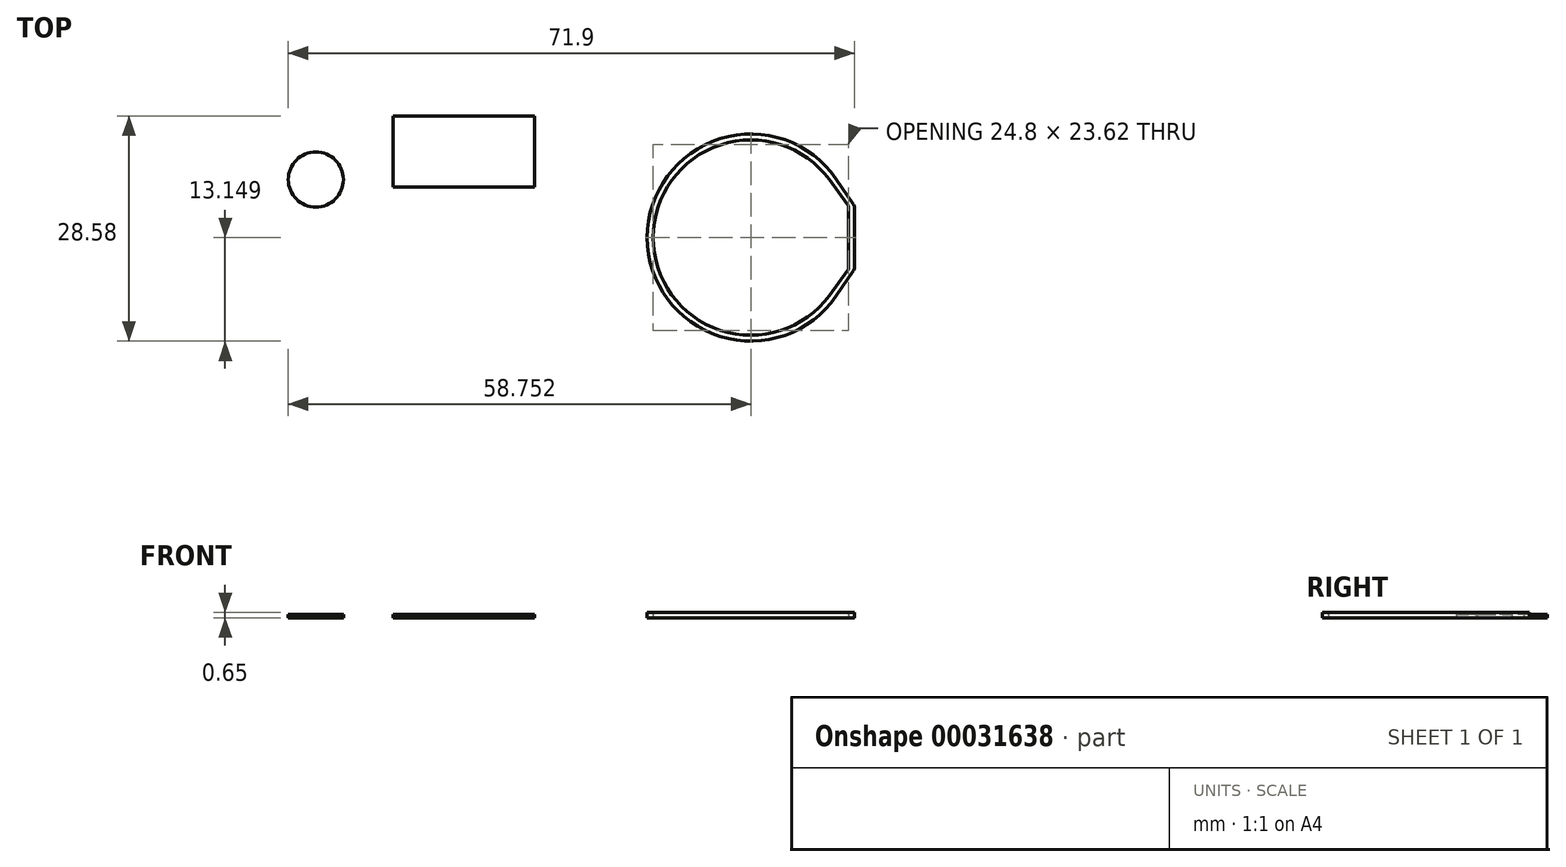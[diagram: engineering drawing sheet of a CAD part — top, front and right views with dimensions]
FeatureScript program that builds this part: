
annotation { "Feature Type Name" : "Feature", "Feature Type Description" : "" }
export const myFeature = defineFeature(function(context is Context, id is Id, definition is map)
    precondition{}
    {
        {
            var Q0;
            Q0=qCreatedBy(makeId("Top.planeOp"),FACE);
            var sketch = newSketch(context, id + "F0", { "sketchPlane" : qUnion([Q0])});
            skCircle(sketch, "E0", {"center": v(-23.37, 19.1) * mm, "radius": 3.5 * mm});
            skLineSegment(sketch, "E1.bottom", {"start": v(-13.56, 27.17) * mm, "end": v(4.44, 27.17) * mm});
            skLineSegment(sketch, "E1.top", {"start": v(-13.56, 18.17) * mm, "end": v(4.44, 18.17) * mm});
            skLineSegment(sketch, "E1.left", {"start": v(-13.56, 27.17) * mm, "end": v(-13.56, 18.17) * mm});
            skLineSegment(sketch, "E1.right", {"start": v(4.44, 27.17) * mm, "end": v(4.44, 18.17) * mm});
            skCircle(sketch, "E2", {"center": v(31.88, 11.74) * mm, "radius": 12.4 * mm});
            skCircle(sketch, "E3", {"center": v(31.88, 11.74) * mm, "radius": 13.15 * mm});
            skLineSegment(sketch, "E4.bottom", {"start": v(44.28, 15.81) * mm, "end": v(45.03, 15.81) * mm});
            skLineSegment(sketch, "E4.top", {"start": v(44.28, 7.66) * mm, "end": v(45.03, 7.66) * mm});
            skLineSegment(sketch, "E4.left", {"start": v(44.28, 15.65) * mm, "end": v(44.28, 7.83) * mm});
            skLineSegment(sketch, "E4.right", {"start": v(45.03, 15.66) * mm, "end": v(45.03, 7.82) * mm});
            skLineSegment(sketch, "E5", {"start": v(44.18, 15.95) * mm, "end": v(41.86, 19.1) * mm});
            skLineSegment(sketch, "E6", {"start": v(44.94, 15.94) * mm, "end": v(42.73, 19.17) * mm});
            skLineSegment(sketch, "E7", {"start": v(44.18, 7.53) * mm, "end": v(41.86, 4.38) * mm});
            skLineSegment(sketch, "E8", {"start": v(44.94, 7.54) * mm, "end": v(42.73, 4.3) * mm});
            skPoint(sketch, "E9.visualSharp", {"position": v(45.03, 15.81) * mm});
            skArc(sketch, "E9.filletArc", {"start": v(45.03, 15.66) * mm, "mid": v(45, 15.8) * mm, "end": v(44.94, 15.94) * mm});
            skPoint(sketch, "E10.visualSharp", {"position": v(45.03, 7.66) * mm});
            skArc(sketch, "E10.filletArc", {"start": v(44.94, 7.54) * mm, "mid": v(45, 7.67) * mm, "end": v(45.03, 7.82) * mm});
            skPoint(sketch, "E11.visualSharp", {"position": v(44.28, 7.66) * mm});
            skArc(sketch, "E11.filletArc", {"start": v(44.18, 7.53) * mm, "mid": v(44.26, 7.67) * mm, "end": v(44.28, 7.83) * mm});
            skPoint(sketch, "E12.visualSharp", {"position": v(44.28, 15.81) * mm});
            skArc(sketch, "E12.filletArc", {"start": v(44.28, 15.65) * mm, "mid": v(44.26, 15.8) * mm, "end": v(44.18, 15.95) * mm});
            skSolve(sketch);
        }
        {
            var Q0;
            Q0=makeQuery(id+"F0.imprint","IMPRINT",FACE,{"disambiguationData":[TD([[makeQuery(id+"F0.imprint","IMPRINT",EDGE,{"derivedFrom":sQuery(id+"F0.wireOp",EDGE,"E0")}),1.0]])]});
            extrude(context, id + "F1", {"entities" : qUnion([Q0]), "depth" : .4 * mm});
        }
        {
            var Q0;
            Q0=makeQuery(id+"F0.imprint","IMPRINT",FACE,{"disambiguationData":[TD([[makeQuery(id+"F0.imprint","IMPRINT",EDGE,{"derivedFrom":sQuery(id+"F0.wireOp",EDGE,"E1.bottom")}),-1.0]])]});
            extrude(context, id + "F2", {"entities" : qUnion([Q0]), "depth" : .4 * mm});
        }
        {
            var Q0;
            {var subQ2=sQuery(id+"F0.wireOp",EDGE,"E5");Q0=makeQuery(id+"F0.imprint","IMPRINT",FACE,{"disambiguationData":[TD([[makeQuery(id+"F0.imprint","IMPRINT",EDGE,{"derivedFrom":subQ2}),-1.0]])]});}
            var Q1;
            {var subQ3=sQuery(id+"F0.wireOp",EDGE,"E6");Q1=makeQuery(id+"F0.imprint","IMPRINT",FACE,{"disambiguationData":[TD([[makeQuery(id+"F0.imprint","IMPRINT",EDGE,{"derivedFrom":subQ3}),1.0]])]});}
            var Q2;
            {var subQ1=sQuery(id+"F0.wireOp",EDGE,"E4.bottom");var subQ5=sQuery(id+"F0.wireOp",EDGE,"E3");var subQ7=makeQuery(id+"F0.imprint","INTERSECT",VERTEX,{"derivedFrom":[subQ5,subQ1]});Q2=makeQuery(id+"F0.imprint","IMPRINT",FACE,{"disambiguationData":[TD([[makeQuery(id+"F0.imprint","IMPRINT",EDGE,{"disambiguationData":[TD([[subQ7,1.0]])],"derivedFrom":subQ5}),-1.0]])]});}
            var Q3;
            {var subQ3=sQuery(id+"F0.wireOp",EDGE,"E4.right");var subQ5=sQuery(id+"F0.wireOp",EDGE,"E3");var subQ6=makeQuery(id+"F0.imprint","INTERSECT",VERTEX,{"derivedFrom":[subQ5,subQ3]});Q3=makeQuery(id+"F0.imprint","IMPRINT",FACE,{"disambiguationData":[TD([[makeQuery(id+"F0.imprint","IMPRINT",EDGE,{"disambiguationData":[TD([[subQ6,1.0]])],"derivedFrom":subQ5}),-1.0]])]});}
            var Q4;
            {var subQ3=sQuery(id+"F0.wireOp",EDGE,"E8");Q4=makeQuery(id+"F0.imprint","IMPRINT",FACE,{"disambiguationData":[TD([[makeQuery(id+"F0.imprint","IMPRINT",EDGE,{"derivedFrom":subQ3}),-1.0]])]});}
            extrude(context, id + "F3", {"entities" : qUnion([Q0, Q1, Q2, Q3, Q4]), "depth" : .65 * mm});
        }
    });
